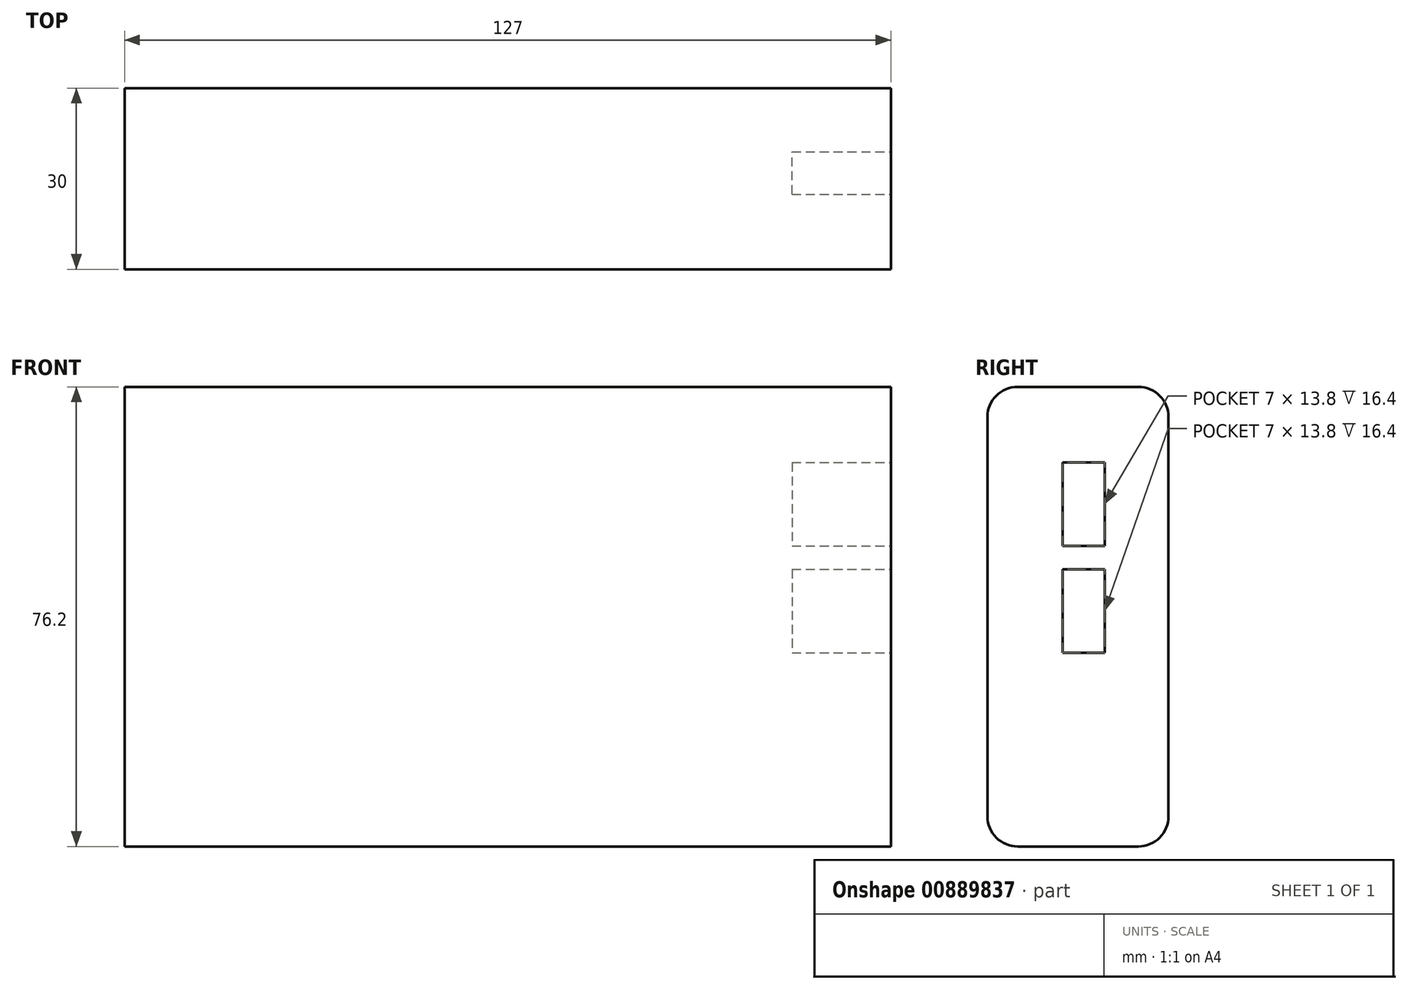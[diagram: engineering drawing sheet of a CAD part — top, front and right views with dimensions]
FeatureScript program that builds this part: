
annotation { "Feature Type Name" : "Feature", "Feature Type Description" : "" }
export const myFeature = defineFeature(function(context is Context, id is Id, definition is map)
    precondition{}
    {
        {
            var Q0;
            Q0=qCreatedBy(makeId("Front.planeOp"),FACE);
            var sketch = newSketch(context, id + "F0", { "sketchPlane" : qUnion([Q0])});
            skLineSegment(sketch, "E0.bottom", {"start": v(63.5, -38.1) * mm, "end": v(-63.5, -38.1) * mm});
            skLineSegment(sketch, "E0.top", {"start": v(63.5, 38.1) * mm, "end": v(-63.5, 38.1) * mm});
            skLineSegment(sketch, "E0.left", {"start": v(63.5, -38.1) * mm, "end": v(63.5, 38.1) * mm});
            skLineSegment(sketch, "E0.right", {"start": v(-63.5, -38.1) * mm, "end": v(-63.5, 38.1) * mm});
            skPoint(sketch, "E0.middle", {"position": v(0, 0) * mm});
            skSolve(sketch);
        }
        {
            var Q0;
            Q0 = qSketchRegion(id + "F0", true);
            extrude(context, id + "F1", {"entities" : qUnion([Q0]), "depth" : 30 * mm, "offsetDistance" : 25 * mm});
        }
        {
            var Q0;
            Q0=makeQuery(id+"F1.opExtrude","CAP_EDGE",EDGE,{"disambiguationData":[OSD([sQuery(id+"F0.wireOp",EDGE,"E0.top")])],"isStart":false});
            var Q1;
            Q1=makeQuery(id+"F1.opExtrude","CAP_EDGE",EDGE,{"disambiguationData":[OSD([sQuery(id+"F0.wireOp",EDGE,"E0.top")])],"isStart":true});
            var Q2;
            Q2=makeQuery(id+"F1.opExtrude","CAP_EDGE",EDGE,{"disambiguationData":[OSD([sQuery(id+"F0.wireOp",EDGE,"E0.bottom")])],"isStart":false});
            var Q3;
            Q3=makeQuery(id+"F1.opExtrude","CAP_EDGE",EDGE,{"disambiguationData":[OSD([sQuery(id+"F0.wireOp",EDGE,"E0.bottom")])],"isStart":true});
            fillet(context, id + "F2", {"entities" : qUnion([Q0, Q1, Q2, Q3]), "radius" : 5 * mm, "tangentPropagation" : true, "allowEdgeOverflow" : false});
        }
        {
            var Q0;
            Q0=makeQuery(id+"F1.opExtrude","SWEPT_FACE",FACE,{"disambiguationData":[OSD([sQuery(id+"F0.wireOp",EDGE,"E0.left")])]});
            var sketch = newSketch(context, id + "F3", { "sketchPlane" : qUnion([Q0])});
            skLineSegment(sketch, "E1.bottom", {"start": v(-17.56, 25.54) * mm, "end": v(-10.56, 25.54) * mm});
            skLineSegment(sketch, "E1.top", {"start": v(-17.56, 11.74) * mm, "end": v(-10.56, 11.74) * mm});
            skLineSegment(sketch, "E1.left", {"start": v(-17.56, 25.54) * mm, "end": v(-17.56, 11.74) * mm});
            skLineSegment(sketch, "E1.right", {"start": v(-10.56, 25.54) * mm, "end": v(-10.56, 11.74) * mm});
            skSolve(sketch);
        }
        {
            var Q0;
            Q0 = qSketchRegion(id + "F3", true);
            extrude(context, id + "F4", {"entities" : qUnion([Q0]), "operationType" : NewBodyOperationType.REMOVE, "oppositeDirection" : true, "depth" : 16.4 * mm, "offsetDistance" : 25 * mm});
        }
        {
            var Q0;
            Q0=makeQuery(id+"F1.opExtrude","SWEPT_FACE",FACE,{"disambiguationData":[OSD([sQuery(id+"F0.wireOp",EDGE,"E0.left")])]});
            var sketch = newSketch(context, id + "F5", { "sketchPlane" : qUnion([Q0])});
            skLineSegment(sketch, "E2.bottom", {"start": v(-17.56, 7.84) * mm, "end": v(-10.56, 7.84) * mm});
            skLineSegment(sketch, "E2.top", {"start": v(-17.56, -5.96) * mm, "end": v(-10.56, -5.96) * mm});
            skLineSegment(sketch, "E2.left", {"start": v(-17.56, 7.84) * mm, "end": v(-17.56, -5.96) * mm});
            skLineSegment(sketch, "E2.right", {"start": v(-10.56, 7.84) * mm, "end": v(-10.56, -5.96) * mm});
            skSolve(sketch);
        }
        {
            var Q0;
            Q0=makeQuery(id+"F5.imprint","IMPRINT",FACE,{"disambiguationData":[TD([[makeQuery(id+"F5.imprint","IMPRINT",EDGE,{"derivedFrom":sQuery(id+"F5.wireOp",EDGE,"E2.bottom")}),-1.0]])]});
            extrude(context, id + "F6", {"entities" : qUnion([Q0]), "operationType" : NewBodyOperationType.REMOVE, "oppositeDirection" : true, "depth" : 16.4 * mm, "offsetDistance" : 25 * mm});
        }
    });
